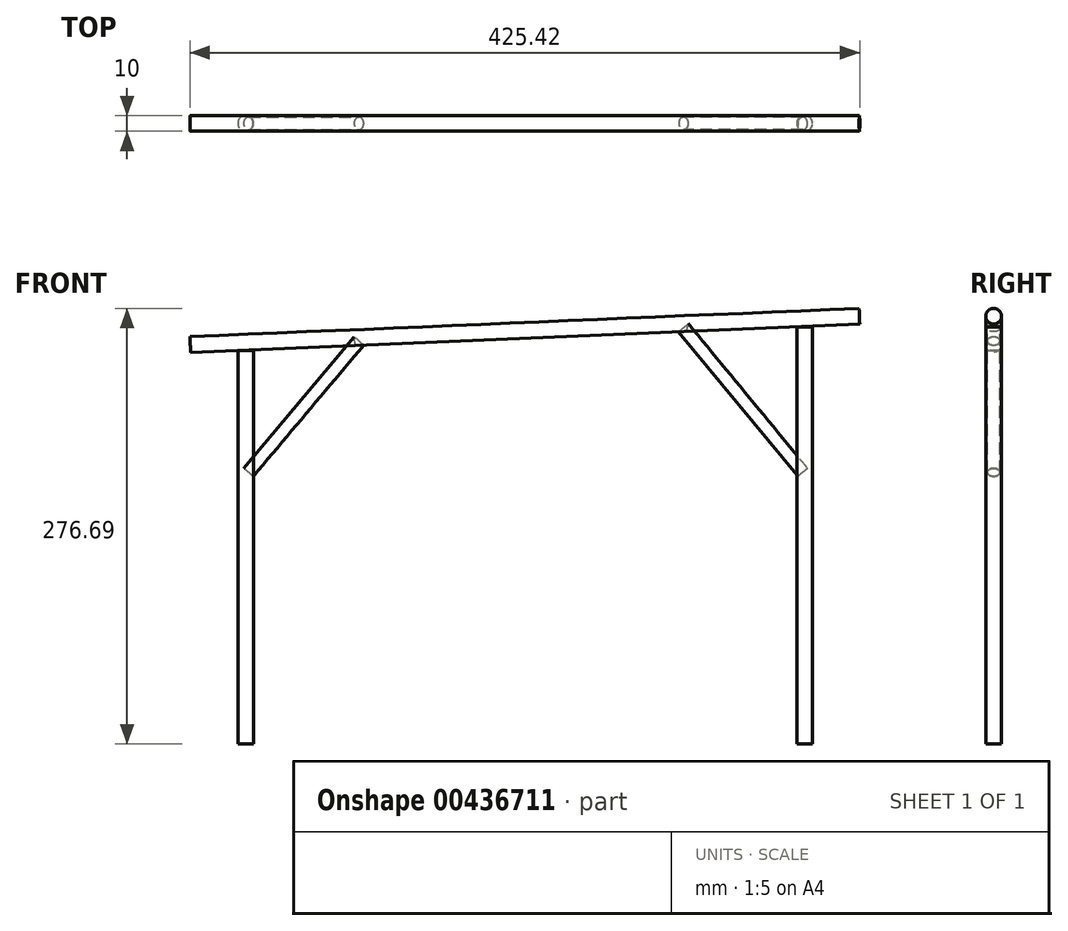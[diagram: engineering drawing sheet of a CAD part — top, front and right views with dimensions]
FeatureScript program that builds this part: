
annotation { "Feature Type Name" : "Feature", "Feature Type Description" : "" }
export const myFeature = defineFeature(function(context is Context, id is Id, definition is map)
    precondition{}
    {
        {
            var Q0;
            Q0=qCreatedBy(makeId("Top.planeOp"),FACE);
            var sketch = newSketch(context, id + "F0", { "sketchPlane" : qUnion([Q0])});
            skCircle(sketch, "E0", {"center": v(0, 0) * mm, "radius": 5 * mm});
            skSolve(sketch);
        }
        {
            var Q0;
            Q0=makeQuery(id+"F0.imprint","IMPRINT",FACE,{"disambiguationData":[TD([[makeQuery(id+"F0.imprint","IMPRINT",EDGE,{"derivedFrom":sQuery(id+"F0.wireOp",EDGE,"E0")}),1.0]])]});
            extrude(context, id + "F1", {"entities" : qUnion([Q0]), "depth" : 265 * mm});
        }
        {
            var Q0;
            Q0=qCreatedBy(makeId("Top.planeOp"),FACE);
            var sketch = newSketch(context, id + "F2", { "sketchPlane" : qUnion([Q0])});
            skCircle(sketch, "E1", {"center": v(-355, 0) * mm, "radius": 5 * mm});
            skSolve(sketch);
        }
        {
            var Q0;
            Q0=makeQuery(id+"F2.imprint","IMPRINT",FACE,{"disambiguationData":[TD([[makeQuery(id+"F2.imprint","IMPRINT",EDGE,{"derivedFrom":sQuery(id+"F2.wireOp",EDGE,"E1")}),1.0]])]});
            extrude(context, id + "F3", {"entities" : qUnion([Q0]), "depth" : 250 * mm});
        }
        {
            var Q0;
            Q0=qCreatedBy(makeId("Front.planeOp"),FACE);
            var sketch = newSketch(context, id + "F4", { "sketchPlane" : qUnion([Q0])});
            skLineSegment(sketch, "E2.0", {"start": v(-360, 250) * mm, "end": v(-350, 250) * mm});
            skLineSegment(sketch, "E3.0", {"start": v(-5, 265) * mm, "end": v(5, 265) * mm});
            skLineSegment(sketch, "E4", {"start": v(-390, 248.73) * mm, "end": v(35, 266.7) * mm});
            skLineSegment(sketch, "E5", {"start": v(-390, 248.73) * mm, "end": v(-390.21, 253.73) * mm});
            skLineSegment(sketch, "E6", {"start": v(35, 266.7) * mm, "end": v(34.79, 271.7) * mm});
            skLineSegment(sketch, "E7", {"start": v(-390.21, 253.73) * mm, "end": v(34.79, 271.7) * mm});
            skSolve(sketch);
        }
        {
            var Q0;
            {var subQ0=sQuery(id+"F4.wireOp",EDGE,"E5");Q0=makeQuery(id+"F4.imprint","IMPRINT",FACE,{"disambiguationData":[TD([[makeQuery(id+"F4.imprint","IMPRINT",EDGE,{"derivedFrom":subQ0}),-1.0]])]});}
            var Q1;
            Q1=sQuery(id+"F4.wireOp",EDGE,"E7");
            revolve(context, id + "F5", {"entities" : qUnion([Q0]), "axis" : qUnion([Q1]), "revolveType" : RevolveType.FULL});
        }
        {
            var Q0;
            Q0=qCreatedBy(makeId("Front.planeOp"),FACE);
            var sketch = newSketch(context, id + "F6", { "sketchPlane" : qUnion([Q0])});
            skLineSegment(sketch, "E8", {"start": v(-371.37, 170) * mm, "end": v(19.43, 170) * mm});
            skLineSegment(sketch, "E9", {"start": v(-280, 305.05) * mm, "end": v(-280, 138.55) * mm});
            skLineSegment(sketch, "E10", {"start": v(-80, 322.32) * mm, "end": v(-80, 122.36) * mm});
            skLineSegment(sketch, "E11.0", {"start": v(-390, 248.73) * mm, "end": v(35, 266.7) * mm});
            skLineSegment(sketch, "E12", {"start": v(-280, 253.38) * mm, "end": v(-350.17, 170) * mm});
            skLineSegment(sketch, "E13.0", {"start": v(-283.06, 255.96) * mm, "end": v(-353.23, 172.58) * mm});
            skLineSegment(sketch, "E14", {"start": v(-80, 261.83) * mm, "end": v(-4.31, 170) * mm});
            skLineSegment(sketch, "E15.0", {"start": v(-76.91, 264.38) * mm, "end": v(-1.23, 172.54) * mm});
            skLineSegment(sketch, "E16", {"start": v(-283.06, 255.96) * mm, "end": v(-280, 253.38) * mm});
            skLineSegment(sketch, "E17", {"start": v(-353.23, 172.58) * mm, "end": v(-350.17, 170) * mm});
            skLineSegment(sketch, "E18", {"start": v(-1.23, 172.54) * mm, "end": v(-4.31, 170) * mm});
            skLineSegment(sketch, "E19", {"start": v(-76.91, 264.38) * mm, "end": v(-80, 261.83) * mm});
            skSolve(sketch);
        }
        {
            var Q0;
            {var subQ0=sQuery(id+"F6.wireOp",EDGE,"E12");Q0=makeQuery(id+"F6.imprint","IMPRINT",FACE,{"disambiguationData":[TD([[makeQuery(id+"F6.imprint","IMPRINT",EDGE,{"derivedFrom":subQ0}),-1.0]])]});}
            var Q1;
            Q1=sQuery(id+"F6.wireOp",EDGE,"E13.0");
            revolve(context, id + "F7", {"entities" : qUnion([Q0]), "axis" : qUnion([Q1]), "revolveType" : RevolveType.FULL});
        }
        {
            var Q0;
            {var subQ0=sQuery(id+"F6.wireOp",EDGE,"E14");Q0=makeQuery(id+"F6.imprint","IMPRINT",FACE,{"disambiguationData":[TD([[makeQuery(id+"F6.imprint","IMPRINT",EDGE,{"derivedFrom":subQ0}),1.0]])]});}
            var Q1;
            Q1=sQuery(id+"F6.wireOp",EDGE,"E15.0");
            revolve(context, id + "F8", {"entities" : qUnion([Q0]), "axis" : qUnion([Q1]), "revolveType" : RevolveType.FULL});
        }
    });
